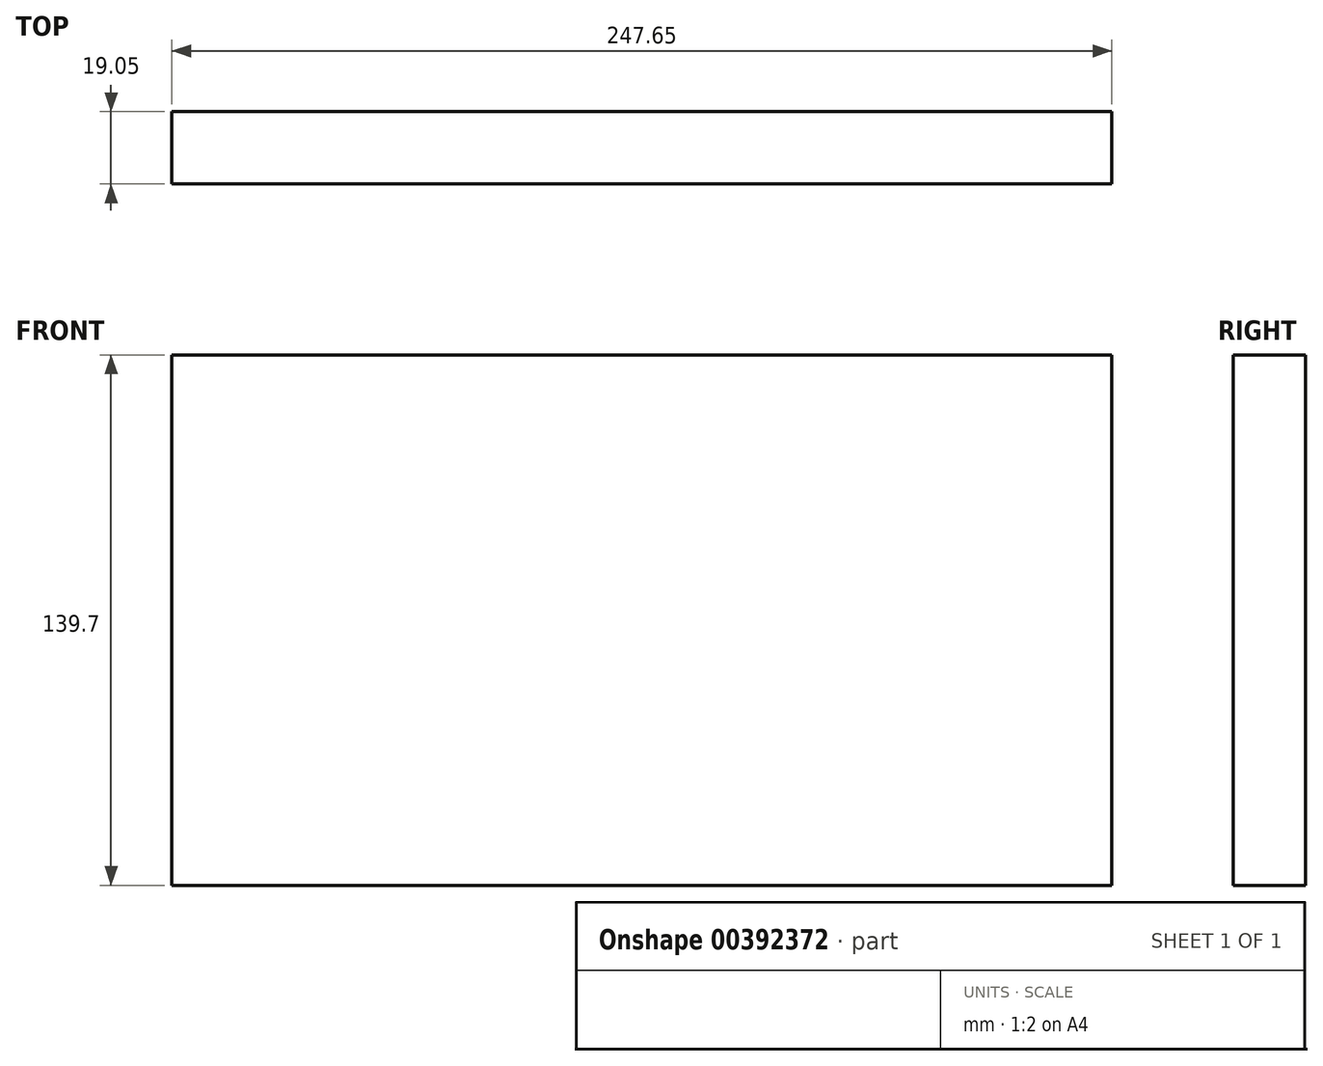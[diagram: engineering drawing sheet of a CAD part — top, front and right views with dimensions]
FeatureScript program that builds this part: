
annotation { "Feature Type Name" : "Feature", "Feature Type Description" : "" }
export const myFeature = defineFeature(function(context is Context, id is Id, definition is map)
    precondition{}
    {
        {
            var Q0;
            Q0=qCreatedBy(makeId("Front.planeOp"),FACE);
            var sketch = newSketch(context, id + "F0", { "sketchPlane" : qUnion([Q0])});
            skLineSegment(sketch, "E0.bottom", {"start": v(-199.75, 0) * mm, "end": v(-447.4, 0) * mm});
            skLineSegment(sketch, "E0.top", {"start": v(-199.75, 139.7) * mm, "end": v(-447.4, 139.7) * mm});
            skLineSegment(sketch, "E0.left", {"start": v(-199.75, 0) * mm, "end": v(-199.75, 139.7) * mm});
            skLineSegment(sketch, "E0.right", {"start": v(-447.4, 0) * mm, "end": v(-447.4, 139.7) * mm});
            skSolve(sketch);
        }
        {
            var Q0;
            Q0=makeQuery(id+"F0.imprint","IMPRINT",FACE,{"disambiguationData":[TD([[makeQuery(id+"F0.imprint","IMPRINT",EDGE,{"derivedFrom":sQuery(id+"F0.wireOp",EDGE,"E0.bottom")}),-1.0]])]});
            extrude(context, id + "F1", {"entities" : qUnion([Q0]), "depth" : 19.05 * mm});
        }
    });
